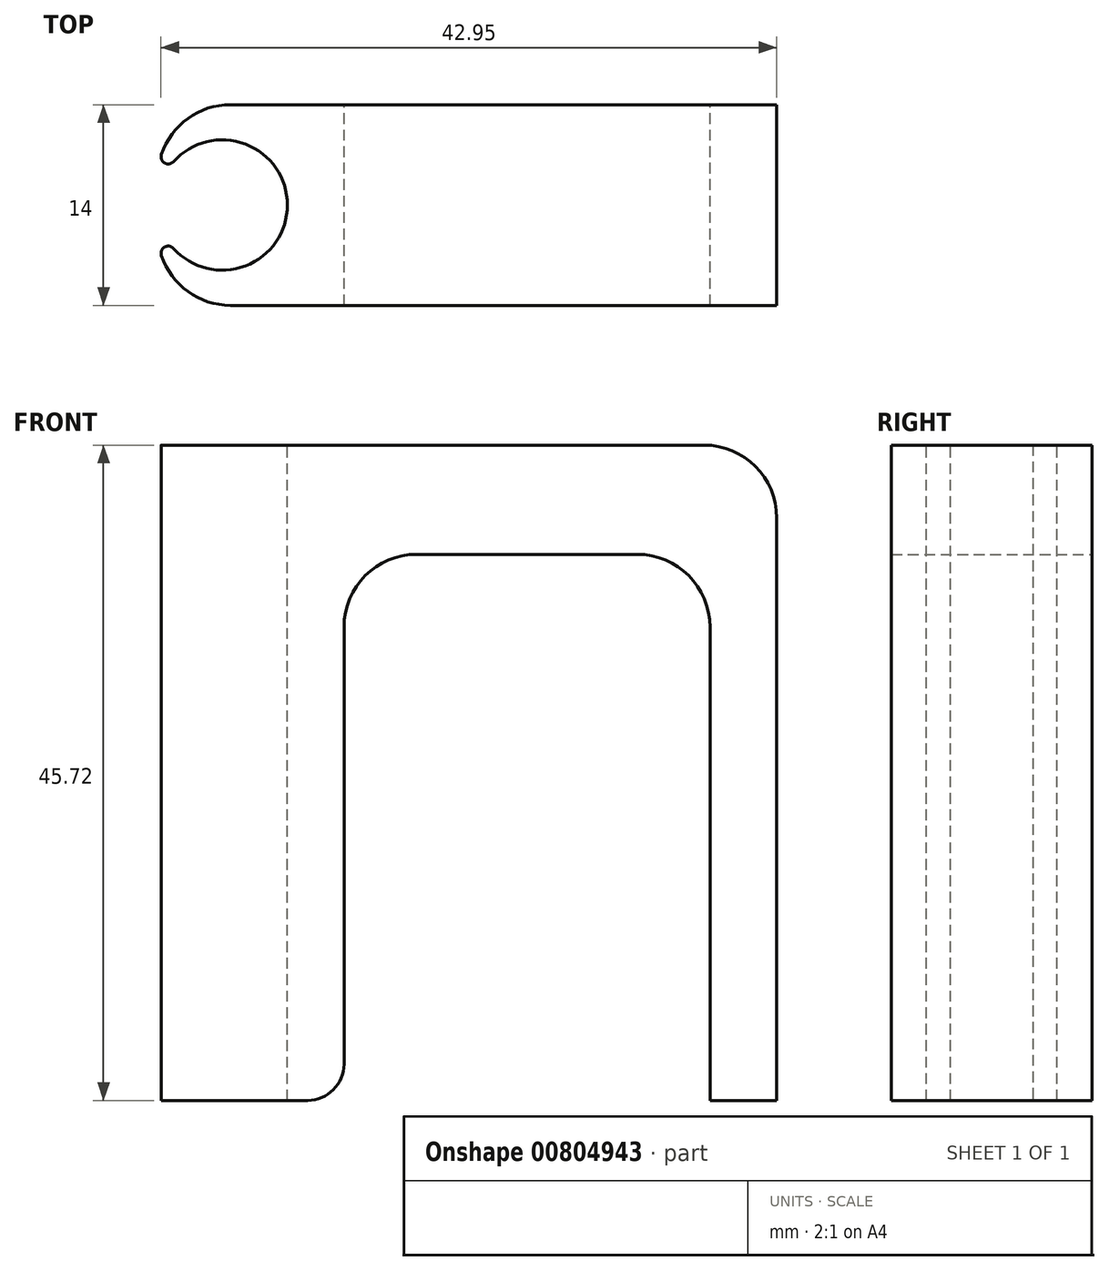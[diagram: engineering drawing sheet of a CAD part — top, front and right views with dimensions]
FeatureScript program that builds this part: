
annotation { "Feature Type Name" : "Feature", "Feature Type Description" : "" }
export const myFeature = defineFeature(function(context is Context, id is Id, definition is map)
    precondition{}
    {
        {
            var Q0;
            Q0=qCreatedBy(makeId("Front.planeOp"),FACE);
            var sketch = newSketch(context, id + "F0", { "sketchPlane" : qUnion([Q0])});
            skLineSegment(sketch, "E0.bottom", {"start": v(-21.6, 22.86) * mm, "end": v(21.59, 22.86) * mm});
            skLineSegment(sketch, "E0.top", {"start": v(-21.6, -22.86) * mm, "end": v(-8.6, -22.86) * mm});
            skLineSegment(sketch, "E0.left", {"start": v(-21.6, 22.86) * mm, "end": v(-21.6, -22.86) * mm});
            skLineSegment(sketch, "E0.right", {"start": v(21.59, 22.86) * mm, "end": v(21.59, -22.86) * mm});
            skPoint(sketch, "E0.middle", {"position": v(0, 0) * mm});
            skLineSegment(sketch, "E1.top", {"start": v(16.94, 15.24) * mm, "end": v(-8.6, 15.24) * mm});
            skLineSegment(sketch, "E1.left", {"start": v(16.94, -22.86) * mm, "end": v(16.94, 15.24) * mm});
            skLineSegment(sketch, "E1.right", {"start": v(-8.6, -22.86) * mm, "end": v(-8.6, 15.24) * mm});
            skLineSegment(sketch, "E2.trimOffspring", {"start": v(16.94, -22.86) * mm, "end": v(21.59, -22.86) * mm});
            skSolve(sketch);
        }
        {
            var Q0;
            Q0 = qSketchRegion(id + "F0", true);
            extrude(context, id + "F1", {"entities" : qUnion([Q0]), "endBound" : BoundingType.SYMMETRIC, "depth" : 14 * mm, "offsetDistance" : 25.4 * mm});
        }
        {
            var Q0;
            Q0=makeQuery(id+"F1.opExtrude","SWEPT_FACE",FACE,{"disambiguationData":[OSD([sQuery(id+"F0.wireOp",EDGE,"E0.bottom")])]});
            var sketch = newSketch(context, id + "F2", { "sketchPlane" : qUnion([Q0])});
            skCircle(sketch, "E3", {"center": v(-17.1, 0) * mm, "radius": 4.55 * mm});
            skSolve(sketch);
        }
        {
            var Q0;
            Q0 = qSketchRegion(id + "F2", true);
            extrude(context, id + "F3", {"entities" : qUnion([Q0]), "operationType" : NewBodyOperationType.REMOVE, "endBound" : BoundingType.THROUGH_ALL, "oppositeDirection" : true, "depth" : 25.4 * mm, "offsetDistance" : 25.4 * mm});
        }
        {
            var Q0;
            Q0=makeQuery(id+"F1.opExtrude","SWEPT_EDGE",EDGE,{"disambiguationData":[OSD([sQuery(id+"F0.wireOp",EDGE,"E1.top"),sQuery(id+"F0.wireOp",EDGE,"E1.right")])]});
            var Q1;
            Q1=makeQuery(id+"F1.opExtrude","SWEPT_EDGE",EDGE,{"disambiguationData":[OSD([sQuery(id+"F0.wireOp",EDGE,"E1.top"),sQuery(id+"F0.wireOp",EDGE,"E1.left")])]});
            var Q2;
            Q2=makeQuery(id+"F1.opExtrude","CAP_EDGE",EDGE,{"disambiguationData":[OSD([sQuery(id+"F0.wireOp",EDGE,"E0.left")])],"isStart":false});
            var Q3;
            Q3=makeQuery(id+"F1.opExtrude","CAP_EDGE",EDGE,{"disambiguationData":[OSD([sQuery(id+"F0.wireOp",EDGE,"E0.left")])],"isStart":true});
            fillet(context, id + "F4", {"entities" : qUnion([Q0, Q1, Q2, Q3]), "radius" : 5.08 * mm, "tangentPropagation" : true, "allowEdgeOverflow" : false});
        }
        {
            var Q0;
            Q0=makeQuery(id+"F3.boolean.opBoolean","INTERSECT",EDGE,{"disambiguationData":[OD(0.0)],"derivedFrom":[makeQuery(id+"F1.opExtrude","SWEPT_FACE",FACE,{"disambiguationData":[OSD([sQuery(id+"F0.wireOp",EDGE,"E0.left")])]}),makeQuery(id+"F3.opExtrude","SWEPT_FACE",FACE,{"disambiguationData":[OSD([sQuery(id+"F2.wireOp",EDGE,"E3")])]})]});
            var Q1;
            Q1=makeQuery(id+"F3.boolean.opBoolean","INTERSECT",EDGE,{"disambiguationData":[OD(1.0)],"derivedFrom":[makeQuery(id+"F1.opExtrude","SWEPT_FACE",FACE,{"disambiguationData":[OSD([sQuery(id+"F0.wireOp",EDGE,"E0.left")])]}),makeQuery(id+"F3.opExtrude","SWEPT_FACE",FACE,{"disambiguationData":[OSD([sQuery(id+"F2.wireOp",EDGE,"E3")])]})]});
            fillet(context, id + "F5", {"entities" : qUnion([Q0, Q1]), "radius" : .5 * mm, "tangentPropagation" : true, "allowEdgeOverflow" : false});
        }
        {
            var Q0;
            Q0=makeQuery(id+"F1.opExtrude","SWEPT_EDGE",EDGE,{"disambiguationData":[OSD([sQuery(id+"F0.wireOp",EDGE,"E0.bottom"),sQuery(id+"F0.wireOp",EDGE,"E0.right")])]});
            fillet(context, id + "F6", {"entities" : qUnion([Q0]), "radius" : 5.08 * mm, "tangentPropagation" : true, "allowEdgeOverflow" : false});
        }
        {
            var Q0;
            Q0=makeQuery(id+"F1.opExtrude","SWEPT_EDGE",EDGE,{"disambiguationData":[OSD([sQuery(id+"F0.wireOp",EDGE,"E0.top"),sQuery(id+"F0.wireOp",EDGE,"E1.right")])]});
            fillet(context, id + "F7", {"entities" : qUnion([Q0]), "radius" : 2.54 * mm, "tangentPropagation" : true, "allowEdgeOverflow" : false});
        }
    });
